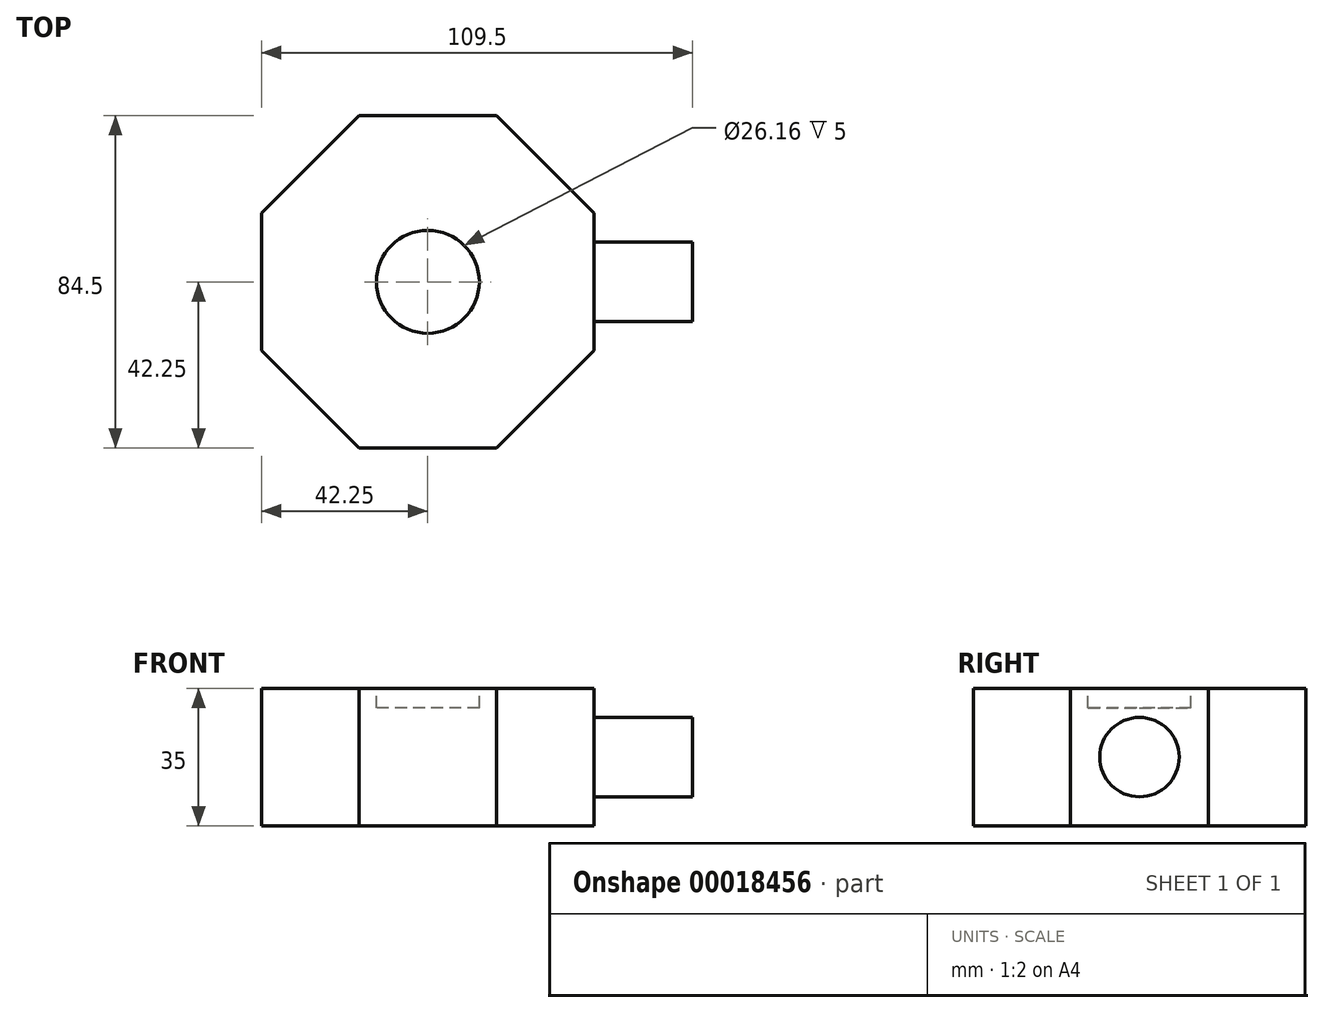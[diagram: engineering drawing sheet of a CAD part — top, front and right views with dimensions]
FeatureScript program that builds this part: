
annotation { "Feature Type Name" : "Feature", "Feature Type Description" : "" }
export const myFeature = defineFeature(function(context is Context, id is Id, definition is map)
    precondition{}
    {
        {
            var Q0;
            Q0=qCreatedBy(makeId("Top.planeOp"),FACE);
            var sketch = newSketch(context, id + "F0", { "sketchPlane" : qUnion([Q0])});
            skCircle(sketch, "E0.cCircle", {"center": v(0, 0) * mm, "radius": 42.25 * mm, "construction": true});
            skLineSegment(sketch, "E0.0", {"start": v(-17.5, 42.25) * mm, "end": v(17.5, 42.25) * mm});
            skLineSegment(sketch, "E0.1", {"start": v(17.5, 42.25) * mm, "end": v(42.25, 17.5) * mm});
            skLineSegment(sketch, "E0.2", {"start": v(42.25, 17.5) * mm, "end": v(42.25, -17.5) * mm});
            skLineSegment(sketch, "E0.3", {"start": v(42.25, -17.5) * mm, "end": v(17.5, -42.25) * mm});
            skLineSegment(sketch, "E0.4", {"start": v(17.5, -42.25) * mm, "end": v(-17.5, -42.25) * mm});
            skLineSegment(sketch, "E0.5", {"start": v(-17.5, -42.25) * mm, "end": v(-42.25, -17.5) * mm});
            skLineSegment(sketch, "E0.6", {"start": v(-42.25, -17.5) * mm, "end": v(-42.25, 17.5) * mm});
            skLineSegment(sketch, "E0.7", {"start": v(-42.25, 17.5) * mm, "end": v(-17.5, 42.25) * mm});
            skPoint(sketch, "E0.0.midPoint", {"position": v(0, 42.25) * mm});
            skSolve(sketch);
        }
        {
            var Q0;
            Q0=makeQuery(id+"F0.imprint","IMPRINT",FACE,{"disambiguationData":[TD([[makeQuery(id+"F0.imprint","IMPRINT",EDGE,{"derivedFrom":sQuery(id+"F0.wireOp",EDGE,"E0.0")}),-1.0]])]});
            extrude(context, id + "F1", {"entities" : qUnion([Q0]), "depth" : 35 * mm});
        }
        {
            var Q0;
            Q0=makeQuery(id+"F1.opExtrude","SWEPT_FACE",FACE,{"disambiguationData":[OSD([sQuery(id+"F0.wireOp",EDGE,"E0.2")])]});
            var sketch = newSketch(context, id + "F2", { "sketchPlane" : qUnion([Q0])});
            skLineSegment(sketch, "E1", {"start": v(0, 0) * mm, "end": v(0, 35) * mm, "construction": true});
            skCircle(sketch, "E2", {"center": v(0, 17.5) * mm, "radius": 10.08 * mm});
            skSolve(sketch);
        }
        {
            var Q0;
            Q0=makeQuery(id+"F1.opExtrude","CAP_FACE",FACE,{"disambiguationData":[OSD([sQuery(id+"F0.wireOp",EDGE,"E0.0"),sQuery(id+"F0.wireOp",EDGE,"E0.1"),sQuery(id+"F0.wireOp",EDGE,"E0.2"),sQuery(id+"F0.wireOp",EDGE,"E0.3"),sQuery(id+"F0.wireOp",EDGE,"E0.4"),sQuery(id+"F0.wireOp",EDGE,"E0.5"),sQuery(id+"F0.wireOp",EDGE,"E0.6"),sQuery(id+"F0.wireOp",EDGE,"E0.7")])],"isStart":false});
            var sketch = newSketch(context, id + "F3", { "sketchPlane" : qUnion([Q0])});
            skCircle(sketch, "E3", {"center": v(0, 0) * mm, "radius": 13.08 * mm});
            skSolve(sketch);
        }
        {
            var Q0;
            Q0=makeQuery(id+"F3.imprint","IMPRINT",FACE,{"disambiguationData":[TD([[makeQuery(id+"F3.imprint","IMPRINT",EDGE,{"derivedFrom":sQuery(id+"F3.wireOp",EDGE,"E3")}),1.0]])]});
            extrude(context, id + "F4", {"entities" : qUnion([Q0]), "operationType" : NewBodyOperationType.REMOVE, "oppositeDirection" : true, "depth" : 5 * mm});
        }
        {
            var Q0;
            Q0=makeQuery(id+"F2.imprint","IMPRINT",FACE,{"disambiguationData":[TD([[makeQuery(id+"F2.imprint","IMPRINT",EDGE,{"derivedFrom":sQuery(id+"F2.wireOp",EDGE,"E2")}),1.0]])]});
            extrude(context, id + "F5", {"entities" : qUnion([Q0]), "operationType" : NewBodyOperationType.ADD, "depth" : 25 * mm});
        }
    });
